# Revit family: Access_Door-Draft_Stop-Best Access Doors-Attic_Application-BA-DSD
name_source: partatom
category: Specialty Equipment
revit_build: Autodesk Revit 2017 (Build: 20160225_1515(x64)
units: mm (PartAtom-declared; Revit-internal decimal feet)

## family parameters
Cut with Voids When Loaded = No
Host = Face
OmniClass Number = 23.30.10.27.17
Part Type = Normal
Room Calculation Point = No
Round Connector Dimension = Use Diameter
Shared = No

## types (1)
- Not a Type - Load Type Catalog
    Assembly Code = C1020700
    Construction Material = Metal - Best Access Doors - Aluminum
    Default Elevation = 0"
    Description = Draft stop access door for attic application
    Door Height Calc = 32"
    Door Width Calc = 32"
    Finish = Metal - Best Access Doors - Powder Coated White
    Frame Depth = 2 1/2"
    Frame Height = 34 1/4"
    Frame Width = 34 1/4"
    Height = 32"
    Manufacturer = Best Access Doors
    Model = BA-DSD
    Product data url = https://bimobject.com
    URL = http://www.bestaccessdoors.com
    Width = 32"

## geometry (parser evidence)
native form markers: Blend x4, Sweep x10
no freeform markers — native parametric forms only
